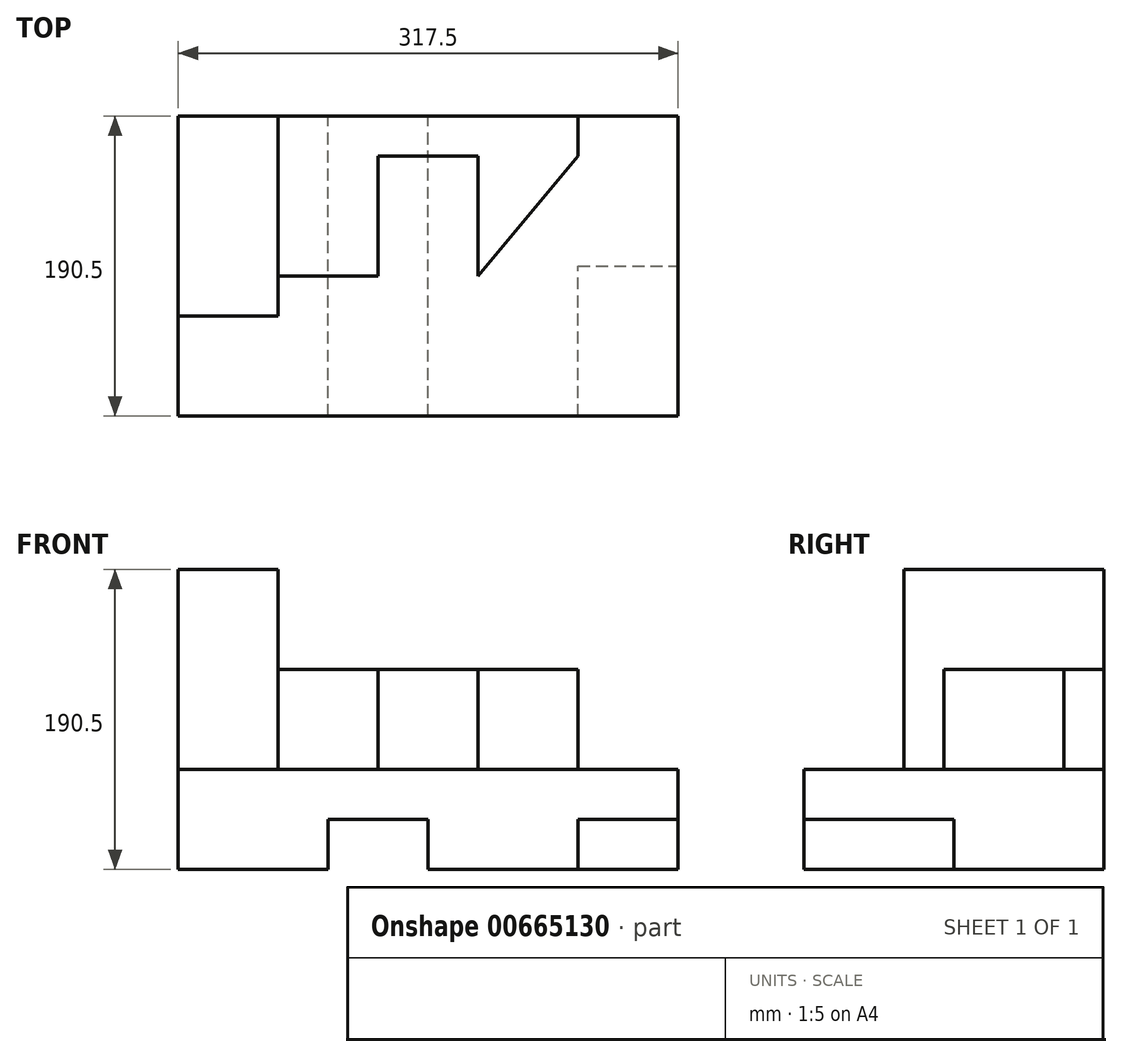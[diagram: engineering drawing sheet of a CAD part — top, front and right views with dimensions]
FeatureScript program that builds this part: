
annotation { "Feature Type Name" : "Feature", "Feature Type Description" : "" }
export const myFeature = defineFeature(function(context is Context, id is Id, definition is map)
    precondition{}
    {
        {
            var Q0;
            Q0=qCreatedBy(makeId("Front.planeOp"),FACE);
            var sketch = newSketch(context, id + "F0", { "sketchPlane" : qUnion([Q0])});
            skLineSegment(sketch, "E0", {"start": v(0, 0) * mm, "end": v(95.25, 0) * mm});
            skLineSegment(sketch, "E1", {"start": v(95.25, 0) * mm, "end": v(95.25, 31.75) * mm});
            skLineSegment(sketch, "E2", {"start": v(95.25, 31.75) * mm, "end": v(158.75, 31.75) * mm});
            skLineSegment(sketch, "E3", {"start": v(158.75, 31.75) * mm, "end": v(158.75, 0) * mm});
            skLineSegment(sketch, "E4", {"start": v(158.75, 0) * mm, "end": v(254, 0) * mm});
            skLineSegment(sketch, "E5", {"start": v(254, 0) * mm, "end": v(254, 31.75) * mm});
            skLineSegment(sketch, "E6", {"start": v(254, 31.75) * mm, "end": v(317.5, 31.75) * mm});
            skLineSegment(sketch, "E7", {"start": v(317.5, 63.5) * mm, "end": v(317.5, 31.75) * mm});
            skLineSegment(sketch, "E8", {"start": v(317.5, 31.75) * mm, "end": v(317.5, 63.5) * mm});
            skLineSegment(sketch, "E9", {"start": v(317.5, 63.5) * mm, "end": v(0, 63.5) * mm});
            skLineSegment(sketch, "E10", {"start": v(0, 63.5) * mm, "end": v(0, 0) * mm});
            skLineSegment(sketch, "E11", {"start": v(317.5, 31.75) * mm, "end": v(317.5, 0) * mm});
            skLineSegment(sketch, "E12", {"start": v(317.5, 0) * mm, "end": v(254, 0) * mm});
            skSolve(sketch);
        }
        {
            var Q0;
            Q0=makeQuery(id+"F0.imprint","IMPRINT",FACE,{"disambiguationData":[TD([[makeQuery(id+"F0.imprint","IMPRINT",EDGE,{"derivedFrom":sQuery(id+"F0.wireOp",EDGE,"E0")}),1.0]])]});
            extrude(context, id + "F1", {"entities" : qUnion([Q0]), "depth" : 95.25 * mm, "offsetDistance" : 25.4 * mm});
        }
        {
            var Q0;
            Q0=makeQuery(id+"F0.imprint","IMPRINT",FACE,{"disambiguationData":[TD([[makeQuery(id+"F0.imprint","IMPRINT",EDGE,{"derivedFrom":sQuery(id+"F0.wireOp",EDGE,"E5")}),-1.0]])]});
            var Q1;
            Q1=makeQuery(id+"F1.opExtrude","CAP_FACE",FACE,{"disambiguationData":[OSD([sQuery(id+"F0.wireOp",EDGE,"E0"),sQuery(id+"F0.wireOp",EDGE,"E1"),sQuery(id+"F0.wireOp",EDGE,"E2"),sQuery(id+"F0.wireOp",EDGE,"E3"),sQuery(id+"F0.wireOp",EDGE,"E4"),sQuery(id+"F0.wireOp",EDGE,"E5"),sQuery(id+"F0.wireOp",EDGE,"E6"),sQuery(id+"F0.wireOp",EDGE,"YTLCEhJ1-Pyti-bSHx-ks0Y-flln8j3Z60Qj"),sQuery(id+"F0.wireOp",EDGE,"E8"),sQuery(id+"F0.wireOp",EDGE,"E9"),sQuery(id+"F0.wireOp",EDGE,"E10")])],"isStart":false});
            extrude(context, id + "F2", {"entities" : qUnion([Q0, Q1]), "operationType" : NewBodyOperationType.ADD, "depth" : 95.25 * mm, "offsetDistance" : 25.4 * mm});
        }
        {
            var Q0;
            {var subQ0=sQuery(id+"F0.wireOp",EDGE,"E9");var subQ1=sQuery(id+"F0.wireOp",EDGE,"YTLCEhJ1-Pyti-bSHx-ks0Y-flln8j3Z60Qj");Q0=makeQuery(id+"F2.boolean.opBoolean","MERGE",FACE,{"derivedFrom":[makeQuery(id+"F1.opExtrude","SWEPT_FACE",FACE,{"disambiguationData":[OSD([subQ1,subQ0])]}),makeQuery(id+"F2.opExtrude","SWEPT_FACE",FACE,{"disambiguationData":[OSD([subQ1,subQ0])]})]});}
            var sketch = newSketch(context, id + "F3", { "sketchPlane" : qUnion([Q0])});
            skLineSegment(sketch, "E13", {"start": v(0, 0) * mm, "end": v(63.5, 0) * mm});
            skLineSegment(sketch, "E14", {"start": v(254, 0) * mm, "end": v(254, -25.4) * mm});
            skLineSegment(sketch, "E15", {"start": v(0, 0) * mm, "end": v(0, -127) * mm});
            skLineSegment(sketch, "E16", {"start": v(0, -127) * mm, "end": v(63.5, -127) * mm});
            skLineSegment(sketch, "E17", {"start": v(63.5, -127) * mm, "end": v(63.5, 0) * mm});
            skLineSegment(sketch, "E18", {"start": v(63.5, -127) * mm, "end": v(63.5, -101.6) * mm});
            skLineSegment(sketch, "E19", {"start": v(63.5, -101.6) * mm, "end": v(127, -101.6) * mm});
            skLineSegment(sketch, "E20", {"start": v(127, -101.6) * mm, "end": v(127, -25.4) * mm});
            skLineSegment(sketch, "E21", {"start": v(127, -25.4) * mm, "end": v(190.5, -25.4) * mm});
            skLineSegment(sketch, "E22", {"start": v(190.5, -25.4) * mm, "end": v(190.5, -101.6) * mm});
            skLineSegment(sketch, "E23", {"start": v(190.5, -101.6) * mm, "end": v(254, -25.4) * mm});
            skLineSegment(sketch, "E24", {"start": v(254, 0) * mm, "end": v(63.5, 0) * mm});
            skSolve(sketch);
        }
        {
            var Q0;
            Q0=makeQuery(id+"F3.imprint","IMPRINT",FACE,{"disambiguationData":[TD([[makeQuery(id+"F3.imprint","IMPRINT",EDGE,{"derivedFrom":sQuery(id+"F3.wireOp",EDGE,"E13")}),1.0]])]});
            extrude(context, id + "F4", {"entities" : qUnion([Q0]), "operationType" : NewBodyOperationType.ADD, "depth" : 127 * mm, "offsetDistance" : 25.4 * mm});
        }
        {
            var Q0;
            Q0=makeQuery(id+"F3.imprint","IMPRINT",FACE,{"disambiguationData":[TD([[makeQuery(id+"F3.imprint","IMPRINT",EDGE,{"derivedFrom":sQuery(id+"F3.wireOp",EDGE,"E14")}),-1.0]])]});
            extrude(context, id + "F5", {"entities" : qUnion([Q0]), "operationType" : NewBodyOperationType.ADD, "depth" : 63.5 * mm, "offsetDistance" : 25.4 * mm});
        }
    });
